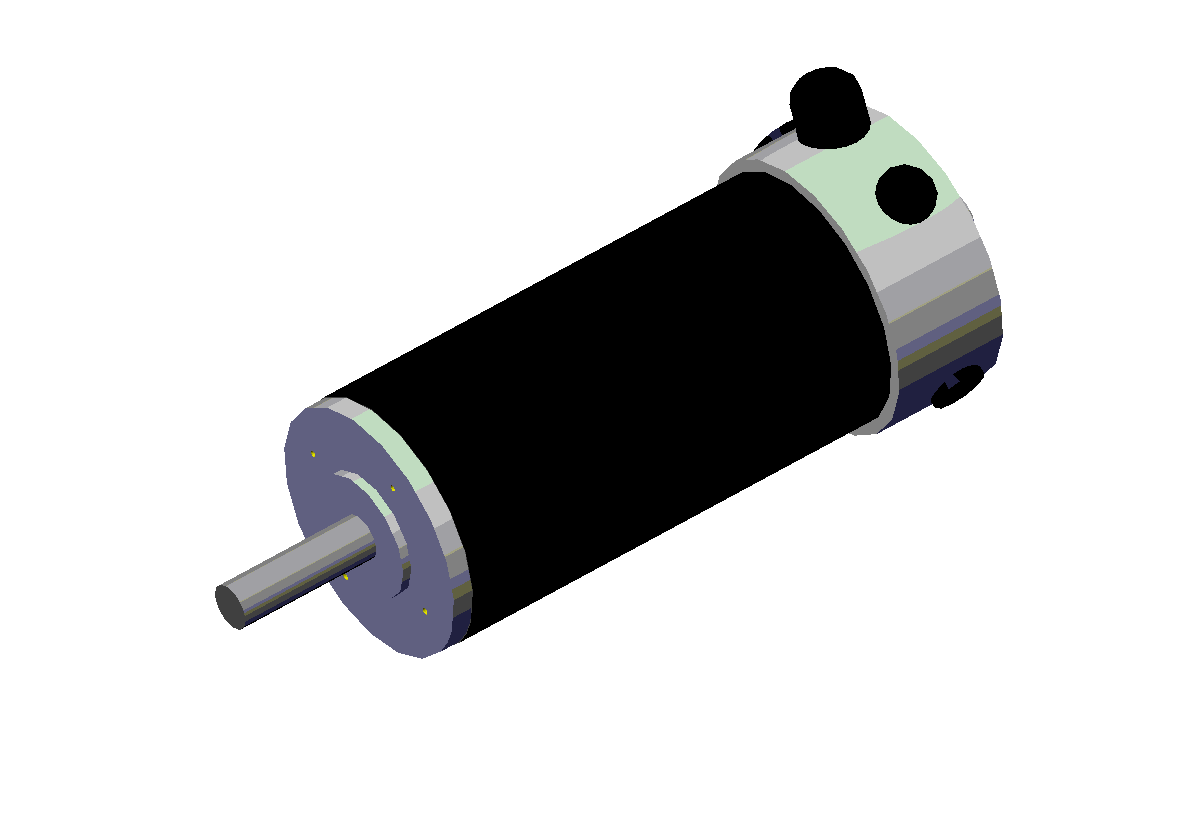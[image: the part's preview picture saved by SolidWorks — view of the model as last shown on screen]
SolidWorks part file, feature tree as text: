
SOLIDWORKS PART (.sldprt)
format: sldprt  version: not decoded by parser v0  size: 121,856 bytes
history: native  units: mm
features: sketch x14, extrude x11, plane x6, fillet x1 (+5 scaffold rows collapsed)
feature tree (37):
  scaffold x5  (default folders/planes/origin — collapsed)
  plane  "Plane1"
  plane  "Plane2"
  plane  "Plane3"
  sketch  "Sketch1"  dims[D1=~4.063954mm]
  extrude  "Base-Extrude"  Depth=165.1mm
  sketch  "Sketch2"  dims[D1=~49.595085mm]
  extrude  "Boss-Extrude1"  Depth=32.766mm
  sketch  "Sketch3"  dims[D1=~8.980256mm]
  extrude  "Boss-Extrude2"  Depth=49.784mm
  sketch  "Sketch4"  dims[D1=~13.73715mm]
  extrude  "Boss-Extrude3"  Depth=8.382mm
  sketch  "Sketch5"
  sketch  "Sketch6"
  plane  "Plane4"
  sketch  "Sketch7"  dims[D1=~9.919017mm]
  extrude  "Boss-Extrude5"  Depth=40.386mm
  sketch  "Sketch9"
  extrude  "Boss-Extrude7"  Depth=80.772mm
  sketch  "Sketch10"
  plane  "Plane5"
  sketch  "Sketch11"  dims[D1=12.5095mm]
  extrude  "Boss-Extrude8"  Depth=40.386mm
  sketch  "Sketch12"  dims[D1=12.5095mm]
  extrude  "Boss-Extrude10"  Depth=80.772mm
  plane  "Plane6"
  sketch  "Sketch13"  dims[D1=36.83mm]
  extrude  "Boss-Extrude11"  Depth=53.975mm
  fillet  "Fillet1"  Radius=6.35mm
  sketch  "Sketch14"  dims[D1=~7.405309mm]
  extrude  "Boss-Extrude12"  Depth=16.002mm
  sketch  "Sketch15"  dims[D1=35.306mm]
  extrude  "Boss-Extrude13"  Depth=5.842mm
decode coverage: 22 of 26 modeling features carry decoded parameters
note: ~ marks probable driven/reference dimensions
note: suppression state not decoded; provenance and decode notes live in map.json
